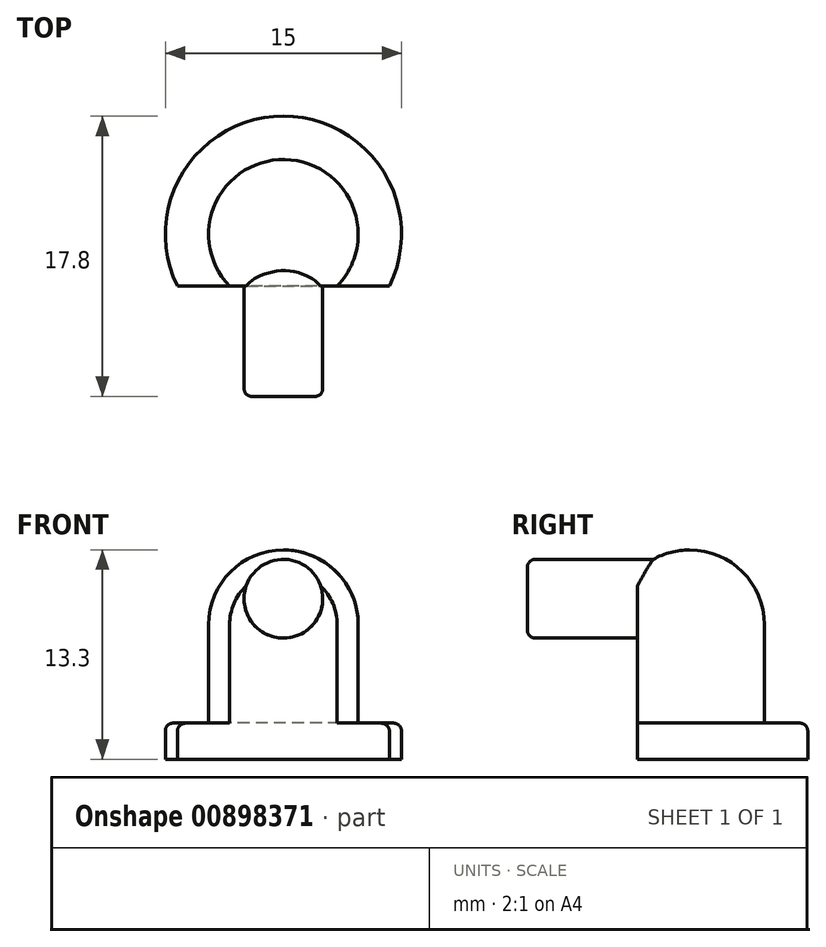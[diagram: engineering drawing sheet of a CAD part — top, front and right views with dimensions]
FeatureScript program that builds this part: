
annotation { "Feature Type Name" : "Feature", "Feature Type Description" : "" }
export const myFeature = defineFeature(function(context is Context, id is Id, definition is map)
    precondition{}
    {
        {
            var Q0;
            Q0=qCreatedBy(makeId("Top.planeOp"),FACE);
            var sketch = newSketch(context, id + "F0", { "sketchPlane" : qUnion([Q0])});
            skCircle(sketch, "E0", {"center": v(0, 0) * mm, "radius": 7.5 * mm});
            skSolve(sketch);
        }
        {
            var Q0;
            Q0=makeQuery(id+"F0.imprint","IMPRINT",FACE,{"disambiguationData":[TD([[makeQuery(id+"F0.imprint","IMPRINT",EDGE,{"derivedFrom":sQuery(id+"F0.wireOp",EDGE,"E0")}),1.0]])]});
            extrude(context, id + "F1", {"entities" : qUnion([Q0]), "depth" : 2.3 * mm, "offsetDistance" : 25 * mm});
        }
        {
            var Q0;
            Q0=makeQuery(id+"F1.opExtrude","CAP_FACE",FACE,{"disambiguationData":[OSD([sQuery(id+"F0.wireOp",EDGE,"E0")])],"isStart":false});
            var sketch = newSketch(context, id + "F2", { "sketchPlane" : qUnion([Q0])});
            skCircle(sketch, "E1", {"center": v(0, 0) * mm, "radius": 4.75 * mm});
            skSolve(sketch);
        }
        {
            var Q0;
            Q0=makeQuery(id+"F2.imprint","IMPRINT",FACE,{"disambiguationData":[TD([[makeQuery(id+"F2.imprint","IMPRINT",EDGE,{"derivedFrom":sQuery(id+"F2.wireOp",EDGE,"E1")}),1.0]])]});
            extrude(context, id + "F3", {"entities" : qUnion([Q0]), "operationType" : NewBodyOperationType.ADD, "depth" : 11 * mm, "offsetDistance" : 25 * mm});
        }
        {
            var Q0;
            Q0=makeQuery(id+"F3.opExtrude","CAP_EDGE",EDGE,{"disambiguationData":[OSD([sQuery(id+"F2.wireOp",EDGE,"E1")])],"isStart":false});
            fillet(context, id + "F4", {"entities" : qUnion([Q0]), "radius" : (9.5 / 2) * mm, "tangentPropagation" : true, "allowEdgeOverflow" : false});
        }
        {
            var Q0;
            Q0=qCreatedBy(makeId("Front.planeOp"),FACE);
            var sketch = newSketch(context, id + "F5", { "sketchPlane" : qUnion([Q0])});
            skLineSegment(sketch, "E2.bottom", {"start": v(13.25, 17.13) * mm, "end": v(-12.53, 17.13) * mm});
            skLineSegment(sketch, "E2.top", {"start": v(13.25, -4.42) * mm, "end": v(-12.53, -4.42) * mm});
            skLineSegment(sketch, "E2.left", {"start": v(13.25, 17.13) * mm, "end": v(13.25, -4.42) * mm});
            skLineSegment(sketch, "E2.right", {"start": v(-12.53, 17.13) * mm, "end": v(-12.53, -4.42) * mm});
            skSolve(sketch);
        }
        {
            var Q0;
            Q0=makeQuery(id+"F5.imprint","IMPRINT",FACE,{"disambiguationData":[TD([[makeQuery(id+"F5.imprint","IMPRINT",EDGE,{"derivedFrom":sQuery(id+"F5.wireOp",EDGE,"E2.bottom")}),1.0]])]});
            extrude(context, id + "F6", {"entities" : qUnion([Q0]), "operationType" : NewBodyOperationType.REMOVE, "endBound" : BoundingType.UP_TO_NEXT, "depth" : 13.5 * mm, "offsetDistance" : 25 * mm, "hasSecondDirection" : true, "secondDirectionOppositeDirection" : false, "secondDirectionDepth" : 3.3 * mm});
        }
        {
            var Q0;
            Q0=makeQuery(id+"F6.boolean.opBoolean","COPY",FACE,{"derivedFrom":makeQuery(id+"F6.opExtrude","CAP_FACE",FACE,{"disambiguationData":[OSD([sQuery(id+"F5.wireOp",EDGE,"E2.bottom"),sQuery(id+"F5.wireOp",EDGE,"E2.top"),sQuery(id+"F5.wireOp",EDGE,"E2.left"),sQuery(id+"F5.wireOp",EDGE,"E2.right")])],"isStart":true})});
            var sketch = newSketch(context, id + "F7", { "sketchPlane" : qUnion([Q0])});
            skCircle(sketch, "E3", {"center": v(0, 10.2) * mm, "radius": 2.5 * mm});
            skSolve(sketch);
        }
        {
            var Q0;
            Q0 = qSketchRegion(id + "F7", true);
            extrude(context, id + "F8", {"entities" : qUnion([Q0]), "operationType" : NewBodyOperationType.ADD, "depth" : 7 * mm, "offsetDistance" : 25 * mm, "hasSecondDirection" : true, "secondDirectionOppositeDirection" : true, "secondDirectionDepth" : 2 * mm});
        }
        {
            var Q0;
            Q0=makeQuery(id+"F1.opExtrude","CAP_EDGE",EDGE,{"disambiguationData":[OSD([sQuery(id+"F0.wireOp",EDGE,"E0")])],"isStart":false});
            fillet(context, id + "F9", {"entities" : qUnion([Q0]), "radius" : 0.5 * mm, "tangentPropagation" : true, "allowEdgeOverflow" : false});
        }
        {
            var Q0;
            Q0=makeQuery(id+"F8.opExtrude","CAP_EDGE",EDGE,{"disambiguationData":[OSD([sQuery(id+"F7.wireOp",EDGE,"E3")])],"isStart":false});
            fillet(context, id + "F10", {"entities" : qUnion([Q0]), "radius" : 0.5 * mm, "tangentPropagation" : true, "allowEdgeOverflow" : false});
        }
    });
